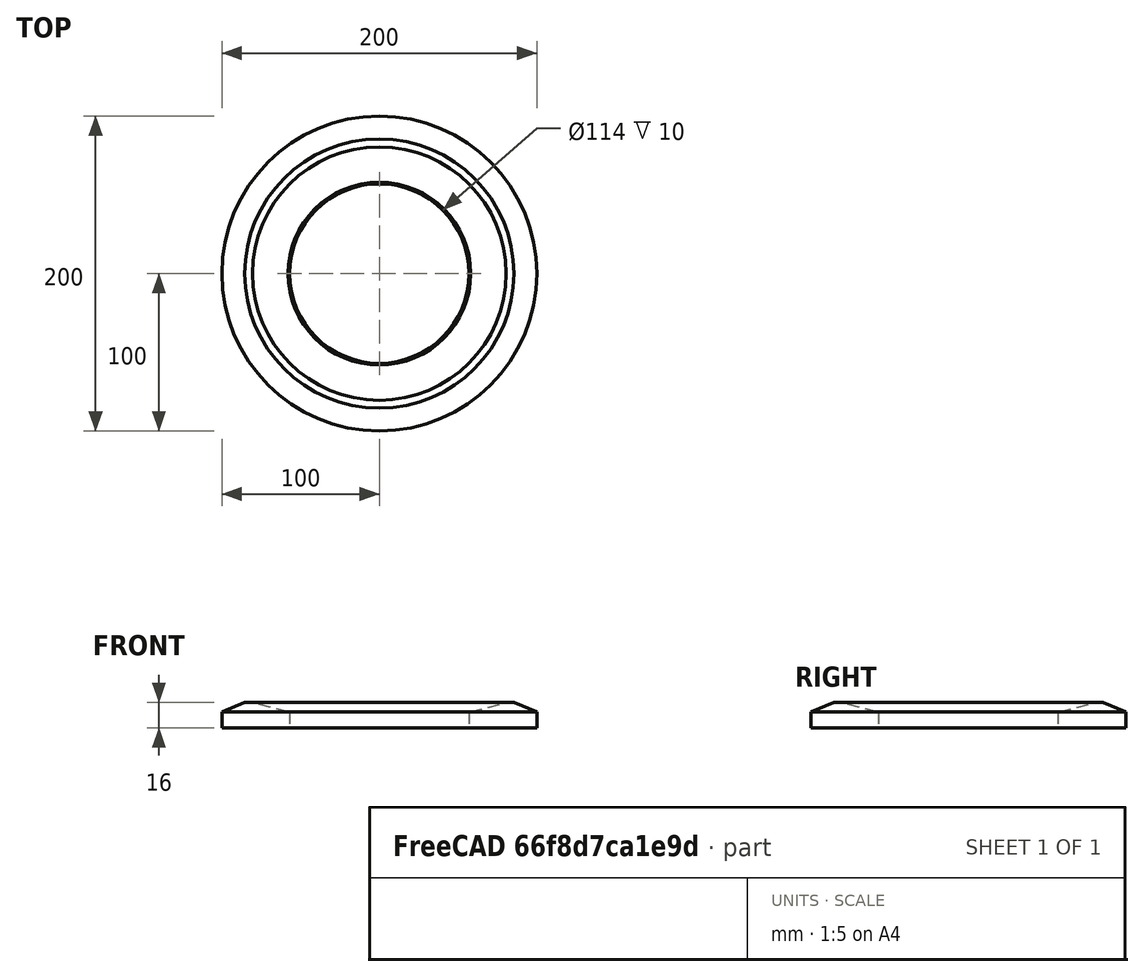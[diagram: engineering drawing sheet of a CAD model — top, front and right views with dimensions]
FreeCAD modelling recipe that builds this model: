
FCSTD DOCUMENT  (FreeCAD 1.0R39109 (Git))
Label: under_lock_bass
License: All rights reserved
LicenseURL: https://en.wikipedia.org/wiki/All_rights_reserved
objects: Sketcher::SketchObject×1, PartDesign::Revolution×1, PartDesign::Body×1
note: 6 computed .brp shape members not serialized (recipe doc carries the construction recipe); baked Part::Feature solids carry a one-line shape summary decoded from their .brp

FEATURE [Sketcher::SketchObject] Sketch
  ArcFitTolerance = 1e-06
  AttachmentSupport = -> [XZ_Plane]
  FullyConstrained = true
  MakeInternals = false
  MapMode = 5
  Placement = pos=(0,0,0) rot=(1,0,0;1.5708rad)
  sketch-geometry (7):
    g0: LineSegment StartX=58 StartY=0 StartZ=0 EndX=80.5 EndY=6 EndZ=0
    g1: LineSegment StartX=80.5 StartY=6 StartZ=0 EndX=85.5 EndY=6 EndZ=0
    g2: LineSegment StartX=85.5 StartY=6 StartZ=0 EndX=100 EndY=0 EndZ=0
    g3: LineSegment StartX=100 StartY=0 StartZ=0 EndX=100 EndY=-10 EndZ=0
    g4: LineSegment StartX=100 StartY=-10 StartZ=0 EndX=57 EndY=-10 EndZ=0
    g5: LineSegment StartX=58 StartY=0 StartZ=0 EndX=57 EndY=0 EndZ=0
    g6: LineSegment StartX=57 StartY=0 StartZ=0 EndX=57 EndY=-10 EndZ=0
  constraints (21):
    c: PointOnObject(g0,g-1)
    c: Coincident(g0,g1)
    c: Horizontal(g1)
    c: Coincident(g1,g2)
    c: PointOnObject(g2,g-1)
    c: Coincident(g2,g3)
    c: DistanceX(g-1,g0) = 80.5
    c: Vertical(g3)
    c: DistanceX(g-1,g0) = 58
    c: DistanceY(g0,g0) = 6
    c: DistanceX(g1,g1) = 5
    c: Distance(g3,g3) = 10
    c: Coincident(g3,g4)
    c: Horizontal(g4)
    c: Coincident(g0,g5)
    c: PointOnObject(g5,g-1)
    c: Coincident(g5,g6)
    c: Coincident(g6,g4)
    c: Vertical(g6)
    c: DistanceX(g-1,g5) = 57
    c: DistanceX(g-1,g3) = 100
FEATURE [PartDesign::Revolution] Revolution
  Angle = 360
  Angle2 = 60
  Axis = (0,2e-16,1)
  Base = (0,0,0)
  Placement = pos=(0,0,0) rot=(1,0,0;1.5708rad)
  Profile = -> Sketch
  ReferenceAxis = -> Sketch [V_Axis]
  Refine = true
  Reversed = true
  Suppressed = false
  Type = 0
FEATURE [PartDesign::Body] Body
  AllowCompound = false
  Group = -> [Sketch,Revolution]
  Origin = -> Origin
  Tip = -> Revolution
